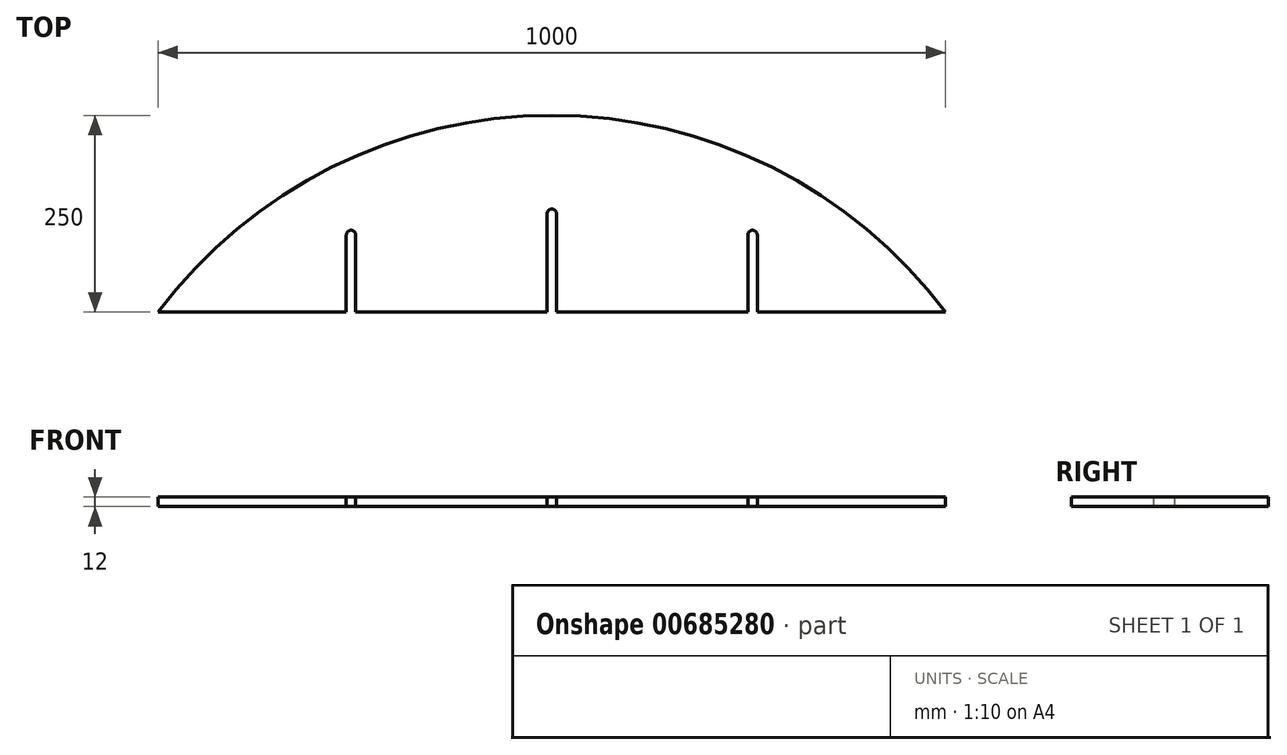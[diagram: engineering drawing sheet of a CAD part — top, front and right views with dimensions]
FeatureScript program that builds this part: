
annotation { "Feature Type Name" : "Feature", "Feature Type Description" : "" }
export const myFeature = defineFeature(function(context is Context, id is Id, definition is map)
    precondition{}
    {
        {
            var Q0;
            Q0=qCreatedBy(makeId("Top.planeOp"),FACE);
            var sketch = newSketch(context, id + "F0", { "sketchPlane" : qUnion([Q0])});
            skLineSegment(sketch, "E0", {"start": v(0, 0) * mm, "end": v(239, 0) * mm});
            skArc(sketch, "E1", {"start": v(1000, 0) * mm, "mid": v(500, 250) * mm, "end": v(0, 0) * mm});
            skLineSegment(sketch, "E2", {"start": v(500, 0) * mm, "end": v(500, 343.75) * mm, "construction": true});
            skLineSegment(sketch, "E3", {"start": v(494, 0) * mm, "end": v(494, 125) * mm});
            skLineSegment(sketch, "E4", {"start": v(506, 125) * mm, "end": v(506, 0) * mm});
            skLineSegment(sketch, "E5.trimOffspring", {"start": v(506, 0) * mm, "end": v(749, 0) * mm});
            skLineSegment(sketch, "E6", {"start": v(755, -21.6) * mm, "end": v(755, 263.34) * mm, "construction": true});
            skLineSegment(sketch, "E7", {"start": v(749, 0) * mm, "end": v(749, 98) * mm});
            skLineSegment(sketch, "E8", {"start": v(761, 98) * mm, "end": v(761, 0) * mm});
            skLineSegment(sketch, "E9.trimOffspring", {"start": v(761, 0) * mm, "end": v(1000, 0) * mm});
            skLineSegment(sketch, "E10.MirrorCS", {"start": v(251, 0) * mm, "end": v(251, 98) * mm});
            skLineSegment(sketch, "E11.MirrorCS", {"start": v(239, 98) * mm, "end": v(239, 0) * mm});
            skLineSegment(sketch, "E12.trimOffspring", {"start": v(251, 0) * mm, "end": v(494, 0) * mm});
            skArc(sketch, "E13", {"start": v(251, 98) * mm, "mid": v(245, 104) * mm, "end": v(239, 98) * mm});
            skArc(sketch, "E14", {"start": v(506, 125) * mm, "mid": v(500, 131) * mm, "end": v(494, 125) * mm});
            skArc(sketch, "E15", {"start": v(761, 98) * mm, "mid": v(755, 104) * mm, "end": v(749, 98) * mm});
            skSolve(sketch);
        }
        {
            var Q0;
            Q0=makeQuery(id+"F0.imprint","IMPRINT",FACE,{"disambiguationData":[TD([[makeQuery(id+"F0.imprint","IMPRINT",EDGE,{"derivedFrom":sQuery(id+"F0.wireOp",EDGE,"E0")}),1.0]])]});
            extrude(context, id + "F1", {"entities" : qUnion([Q0]), "depth" : 12 * mm, "offsetDistance" : 25 * mm});
        }
    });
